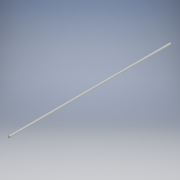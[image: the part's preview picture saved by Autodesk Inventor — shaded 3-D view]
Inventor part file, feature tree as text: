
AUTODESK INVENTOR PART (.ipt)
format: ipt  version: 2019 (Build 230136000, 136)  size: 89,600 bytes
history: native  units: mm
features: extrude x1, sketch x1
ambient origin geometry x8: Origin, YZ Plane, XZ Plane, XY Plane, X Axis, Y Axis, Z Axis, Center Point
bodies: Solid1 (feature_tree)
feature tree (2):
  extrude  "Extrusion1"  Depth=296.0mm TaperAngle=0.0deg
  sketch  "Sketch1"  dims[d0=3.0mm d1=296.0mm d2=0.0mm]
